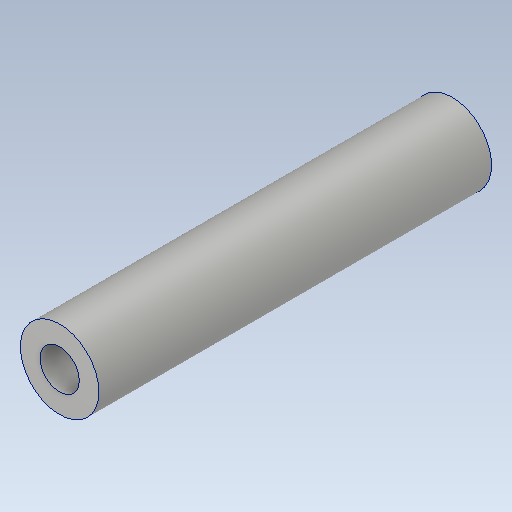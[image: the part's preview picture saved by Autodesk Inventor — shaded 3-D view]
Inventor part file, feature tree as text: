
AUTODESK INVENTOR PART (.ipt)
format: ipt  version: 2020.2 (Build 242310000, 310)  size: 114,176 bytes
history: native  units: mm
features: sketch x2, extrude x2, hole x2, other x1
ambient origin geometry x8: Origin, YZ Plane, XZ Plane, XY Plane, X Axis, Y Axis, Z Axis, Center Point
bodies: Body1 (feature_tree)
feature tree (7):
  other  "ソリッド1"
  sketch  "スケッチ1"
  extrude  "押し出し1"  Depth=8.0mm
  sketch  "スケッチ2"
  extrude  "押し出し2"  Depth=4.001mm
  hole  "穴1"  [1 undecoded]
  hole  "穴2"  [1 undecoded]
note: 2 required parameter values undecoded (feature->parameter linkage not recoverable at this tier; creation-order binding heuristic only, values carry confidence <= 0.55)
